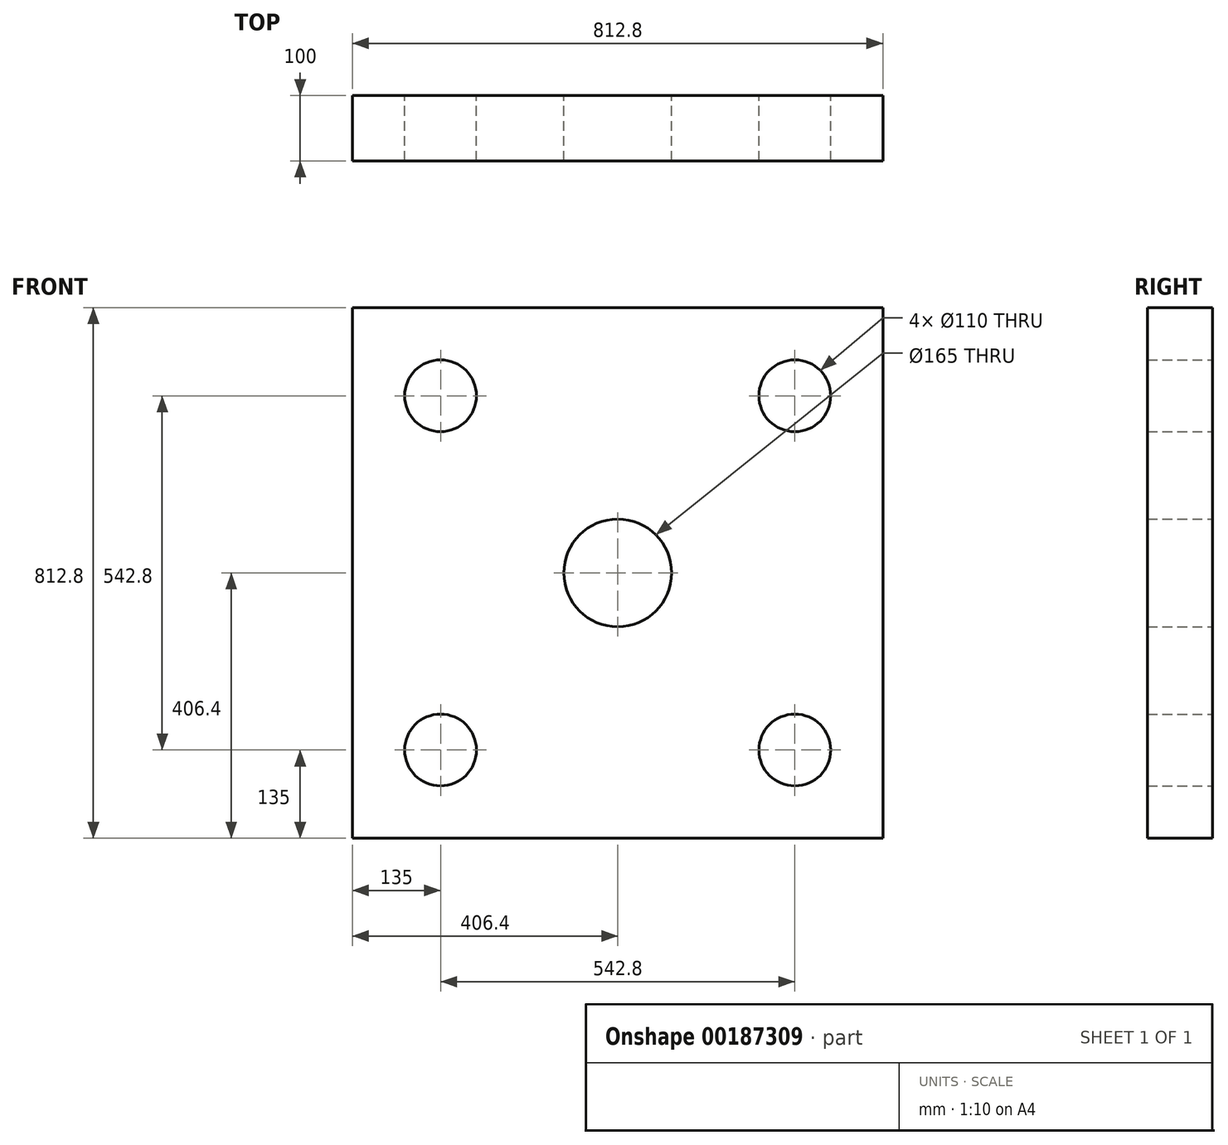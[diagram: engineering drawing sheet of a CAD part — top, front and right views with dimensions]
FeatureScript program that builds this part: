
annotation { "Feature Type Name" : "Feature", "Feature Type Description" : "" }
export const myFeature = defineFeature(function(context is Context, id is Id, definition is map)
    precondition{}
    {
        {
            var Q0;
            Q0=qCreatedBy(makeId("Front.planeOp"),FACE);
            var sketch = newSketch(context, id + "F0", { "sketchPlane" : qUnion([Q0])});
            skLineSegment(sketch, "E0.bottom", {"start": v(-406.4, -406.4) * mm, "end": v(406.4, -406.4) * mm});
            skLineSegment(sketch, "E0.top", {"start": v(-406.4, 406.4) * mm, "end": v(406.4, 406.4) * mm});
            skLineSegment(sketch, "E0.left", {"start": v(-406.4, -406.4) * mm, "end": v(-406.4, 406.4) * mm});
            skLineSegment(sketch, "E0.right", {"start": v(406.4, -406.4) * mm, "end": v(406.4, 406.4) * mm});
            skPoint(sketch, "E0.middle", {"position": v(0, 0) * mm});
            skLineSegment(sketch, "E1", {"start": v(-271.4, 435.08) * mm, "end": v(-271.4, -466.79) * mm, "construction": true});
            skLineSegment(sketch, "E2", {"start": v(271.4, 435.63) * mm, "end": v(271.4, -467.34) * mm, "construction": true});
            skLineSegment(sketch, "E3", {"start": v(-482.99, 271.4) * mm, "end": v(474.5, 271.4) * mm, "construction": true});
            skLineSegment(sketch, "E4", {"start": v(-470.32, -271.4) * mm, "end": v(478.3, -271.4) * mm, "construction": true});
            skCircle(sketch, "E5", {"center": v(-271.4, 271.4) * mm, "radius": 55 * mm});
            skLineSegment(sketch, "E6", {"start": v(-420.18, 0) * mm, "end": v(457.83, 0) * mm, "construction": true});
            skCircle(sketch, "E7.MirrorC", {"center": v(-271.4, -271.4) * mm, "radius": 55 * mm});
            skLineSegment(sketch, "E8", {"start": v(0, 436.93) * mm, "end": v(0, -451.52) * mm, "construction": true});
            skCircle(sketch, "E9.MirrorC", {"center": v(271.4, -271.4) * mm, "radius": 55 * mm});
            skCircle(sketch, "E10.MirrorC", {"center": v(271.4, 271.4) * mm, "radius": 55 * mm});
            skCircle(sketch, "E11", {"center": v(0, 0) * mm, "radius": 82.5 * mm});
            skSolve(sketch);
        }
        {
            var Q0;
            Q0 = qSketchRegion(id + "F0", true);
            extrude(context, id + "F1", {"entities" : qUnion([Q0]), "depth" : 100 * mm});
        }
    });
